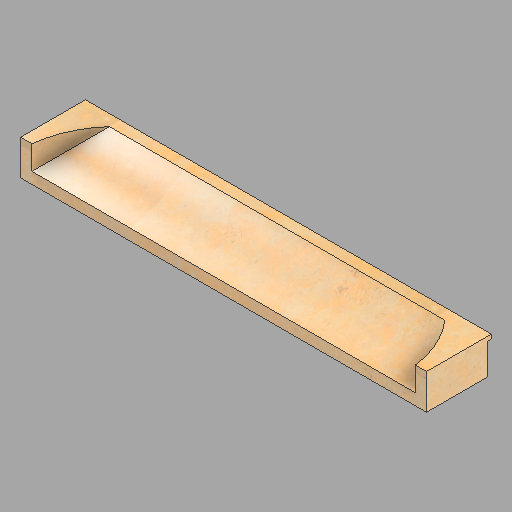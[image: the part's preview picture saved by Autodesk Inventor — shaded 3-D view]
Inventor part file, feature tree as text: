
AUTODESK INVENTOR PART (.ipt)
format: ipt  version: 2022.2 (Build 262287010, 287A)  size: 229,888 bytes
history: native  units: in
note: dims shown in document units (in); Inventor stores cm internally (conversion verified against a paired STEP export)
features: revolve x2, other x1, direct_edit x1
ambient origin geometry x8: Origin, YZ Plane, XZ Plane, XY Plane, X Axis, Y Axis, Z Axis, Center Point
bodies: Solid1 (feature_tree)
feature tree (4):
  other  "West (2)"
  direct_edit  "Direct Edit1"
  revolve  "Rotate1"  [1 undecoded]
  revolve  "Rotate2"  Angle=90.0deg
note: 1 required parameter value undecoded (feature->parameter linkage not recoverable at this tier; creation-order binding heuristic only, values carry confidence <= 0.55)
